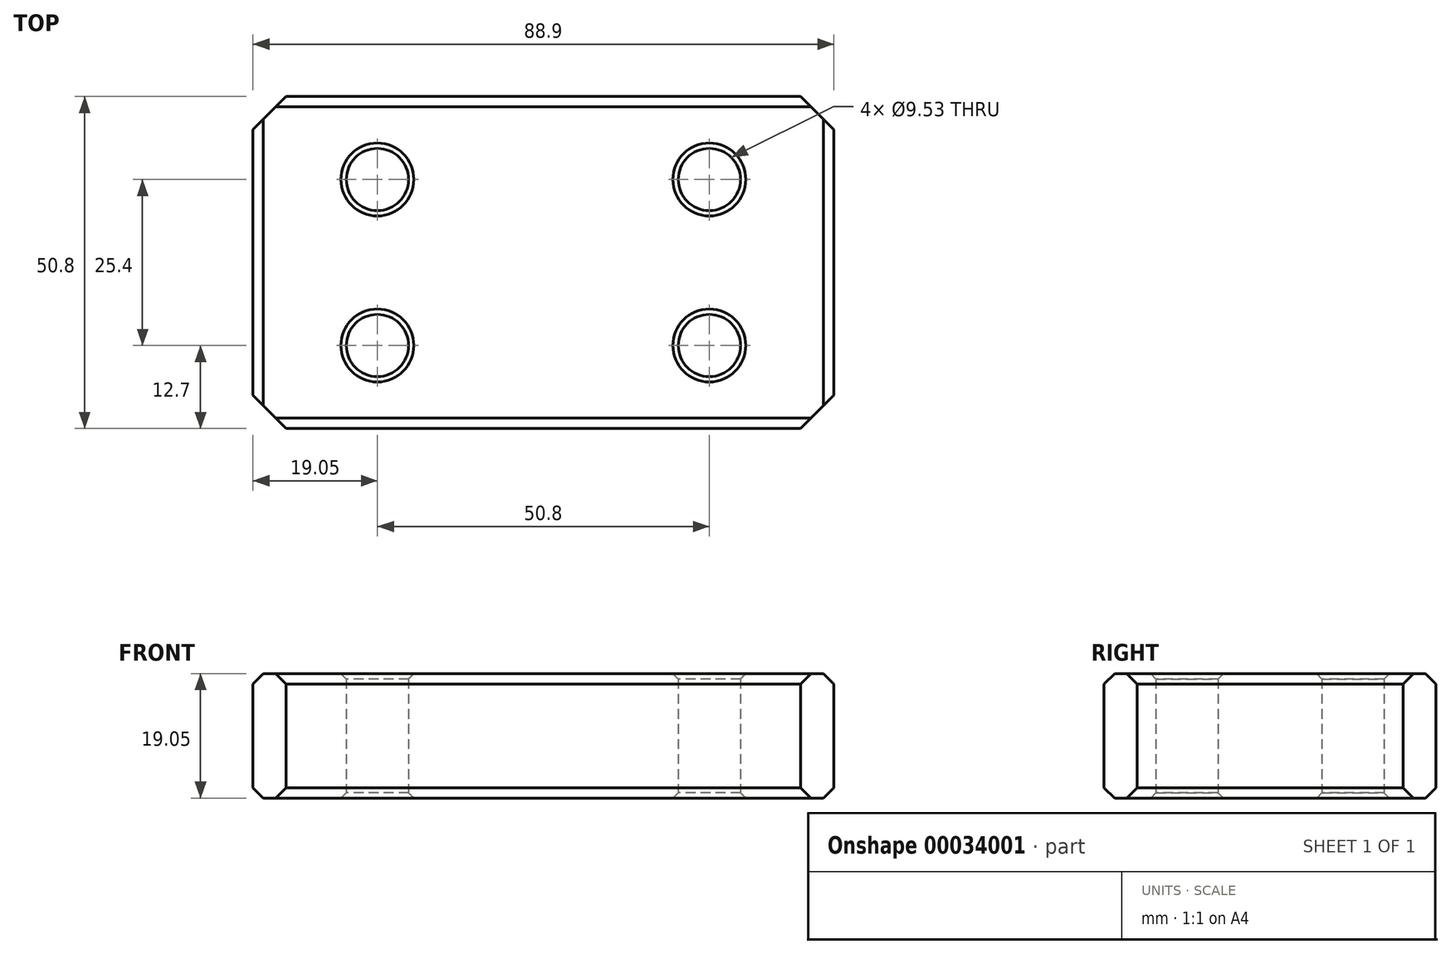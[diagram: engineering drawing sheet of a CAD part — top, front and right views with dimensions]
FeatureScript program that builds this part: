
annotation { "Feature Type Name" : "Feature", "Feature Type Description" : "" }
export const myFeature = defineFeature(function(context is Context, id is Id, definition is map)
    precondition{}
    {
        {
            var Q0;
            Q0=qCreatedBy(makeId("Top.planeOp"),FACE);
            var sketch = newSketch(context, id + "F0", { "sketchPlane" : qUnion([Q0])});
            skLineSegment(sketch, "E0.rect.bottom", {"start": v(44.45, -25.4) * mm, "end": v(-44.45, -25.4) * mm});
            skLineSegment(sketch, "E0.rect.top", {"start": v(44.45, 25.4) * mm, "end": v(-44.45, 25.4) * mm});
            skLineSegment(sketch, "E0.rect.left", {"start": v(44.45, -25.4) * mm, "end": v(44.45, 25.4) * mm});
            skLineSegment(sketch, "E0.rect.right", {"start": v(-44.45, -25.4) * mm, "end": v(-44.45, 25.4) * mm});
            skPoint(sketch, "E0.rect.middle", {"position": v(0, 0) * mm});
            skCircle(sketch, "E1", {"center": v(-25.4, 12.7) * mm, "radius": 4.76 * mm});
            skCircle(sketch, "E2", {"center": v(25.4, 12.7) * mm, "radius": 4.76 * mm});
            skCircle(sketch, "E3", {"center": v(-25.4, -12.7) * mm, "radius": 4.76 * mm});
            skCircle(sketch, "E4", {"center": v(25.4, -12.7) * mm, "radius": 4.76 * mm});
            skSolve(sketch);
        }
        {
            var Q0;
            Q0 = qSketchRegion(id + "F0", true);
            extrude(context, id + "F1", {"entities" : qUnion([Q0]), "depth" : 19.05 * mm});
        }
        {
            var Q0;
            Q0=makeQuery(id+"F1.opExtrude","SWEPT_EDGE",EDGE,{"disambiguationData":[OSD([sQuery(id+"F0.wireOp",EDGE,"E0.rect.bottom"),sQuery(id+"F0.wireOp",EDGE,"E0.rect.left")])]});
            var Q1;
            Q1=makeQuery(id+"F1.opExtrude","SWEPT_EDGE",EDGE,{"disambiguationData":[OSD([sQuery(id+"F0.wireOp",EDGE,"E0.rect.top"),sQuery(id+"F0.wireOp",EDGE,"E0.rect.left")])]});
            var Q2;
            Q2=makeQuery(id+"F1.opExtrude","SWEPT_EDGE",EDGE,{"disambiguationData":[OSD([sQuery(id+"F0.wireOp",EDGE,"E0.rect.top"),sQuery(id+"F0.wireOp",EDGE,"E0.rect.right")])]});
            var Q3;
            Q3=makeQuery(id+"F1.opExtrude","SWEPT_EDGE",EDGE,{"disambiguationData":[OSD([sQuery(id+"F0.wireOp",EDGE,"E0.rect.bottom"),sQuery(id+"F0.wireOp",EDGE,"E0.rect.right")])]});
            chamfer(context, id + "F2", {"entities" : qUnion([Q0, Q1, Q2, Q3]), "width" : 5.08 * mm, "tangentPropagation" : true});
        }
        {
            var Q0;
            Q0=makeQuery(id+"F1.opExtrude","CAP_EDGE",EDGE,{"disambiguationData":[OSD([sQuery(id+"F0.wireOp",EDGE,"E1")])],"isStart":false});
            var Q1;
            Q1=makeQuery(id+"F1.opExtrude","CAP_EDGE",EDGE,{"disambiguationData":[OSD([sQuery(id+"F0.wireOp",EDGE,"E1")])],"isStart":true});
            var Q2;
            Q2=makeQuery(id+"F1.opExtrude","CAP_EDGE",EDGE,{"disambiguationData":[OSD([sQuery(id+"F0.wireOp",EDGE,"E2")])],"isStart":false});
            var Q3;
            Q3=makeQuery(id+"F1.opExtrude","CAP_EDGE",EDGE,{"disambiguationData":[OSD([sQuery(id+"F0.wireOp",EDGE,"E2")])],"isStart":true});
            var Q4;
            Q4=makeQuery(id+"F1.opExtrude","CAP_EDGE",EDGE,{"disambiguationData":[OSD([sQuery(id+"F0.wireOp",EDGE,"E4")])],"isStart":false});
            var Q5;
            Q5=makeQuery(id+"F1.opExtrude","CAP_EDGE",EDGE,{"disambiguationData":[OSD([sQuery(id+"F0.wireOp",EDGE,"E4")])],"isStart":true});
            var Q6;
            Q6=makeQuery(id+"F1.opExtrude","CAP_EDGE",EDGE,{"disambiguationData":[OSD([sQuery(id+"F0.wireOp",EDGE,"E3")])],"isStart":false});
            var Q7;
            Q7=makeQuery(id+"F1.opExtrude","CAP_EDGE",EDGE,{"disambiguationData":[OSD([sQuery(id+"F0.wireOp",EDGE,"E3")])],"isStart":true});
            chamfer(context, id + "F3", {"entities" : qUnion([Q0, Q1, Q2, Q3, Q4, Q5, Q6, Q7]), "width" : 0.81 * mm, "tangentPropagation" : true});
        }
        {
            var Q0;
            Q0=makeQuery(id+"F1.opExtrude","CAP_EDGE",EDGE,{"disambiguationData":[OSD([sQuery(id+"F0.wireOp",EDGE,"E0.rect.bottom")])],"isStart":false});
            var Q1;
            Q1=makeQuery(id+"F1.opExtrude","CAP_EDGE",EDGE,{"disambiguationData":[OSD([sQuery(id+"F0.wireOp",EDGE,"E0.rect.right")])],"isStart":false});
            var Q2;
            Q2=makeQuery(id+"F1.opExtrude","CAP_EDGE",EDGE,{"disambiguationData":[OSD([sQuery(id+"F0.wireOp",EDGE,"E0.rect.top")])],"isStart":false});
            var Q3;
            Q3=makeQuery(id+"F1.opExtrude","CAP_EDGE",EDGE,{"disambiguationData":[OSD([sQuery(id+"F0.wireOp",EDGE,"E0.rect.right")])],"isStart":true});
            var Q4;
            Q4=makeQuery(id+"F1.opExtrude","CAP_EDGE",EDGE,{"disambiguationData":[OSD([sQuery(id+"F0.wireOp",EDGE,"E0.rect.bottom")])],"isStart":true});
            var Q5;
            Q5=makeQuery(id+"F1.opExtrude","CAP_EDGE",EDGE,{"disambiguationData":[OSD([sQuery(id+"F0.wireOp",EDGE,"E0.rect.left")])],"isStart":false});
            var Q6;
            Q6=makeQuery(id+"F1.opExtrude","CAP_EDGE",EDGE,{"disambiguationData":[OSD([sQuery(id+"F0.wireOp",EDGE,"E0.rect.left")])],"isStart":true});
            var Q7;
            Q7=makeQuery(id+"F1.opExtrude","CAP_EDGE",EDGE,{"disambiguationData":[OSD([sQuery(id+"F0.wireOp",EDGE,"E0.rect.top")])],"isStart":true});
            chamfer(context, id + "F4", {"entities" : qUnion([Q0, Q1, Q2, Q3, Q4, Q5, Q6, Q7]), "width" : 1.6 * mm, "tangentPropagation" : true});
        }
    });
